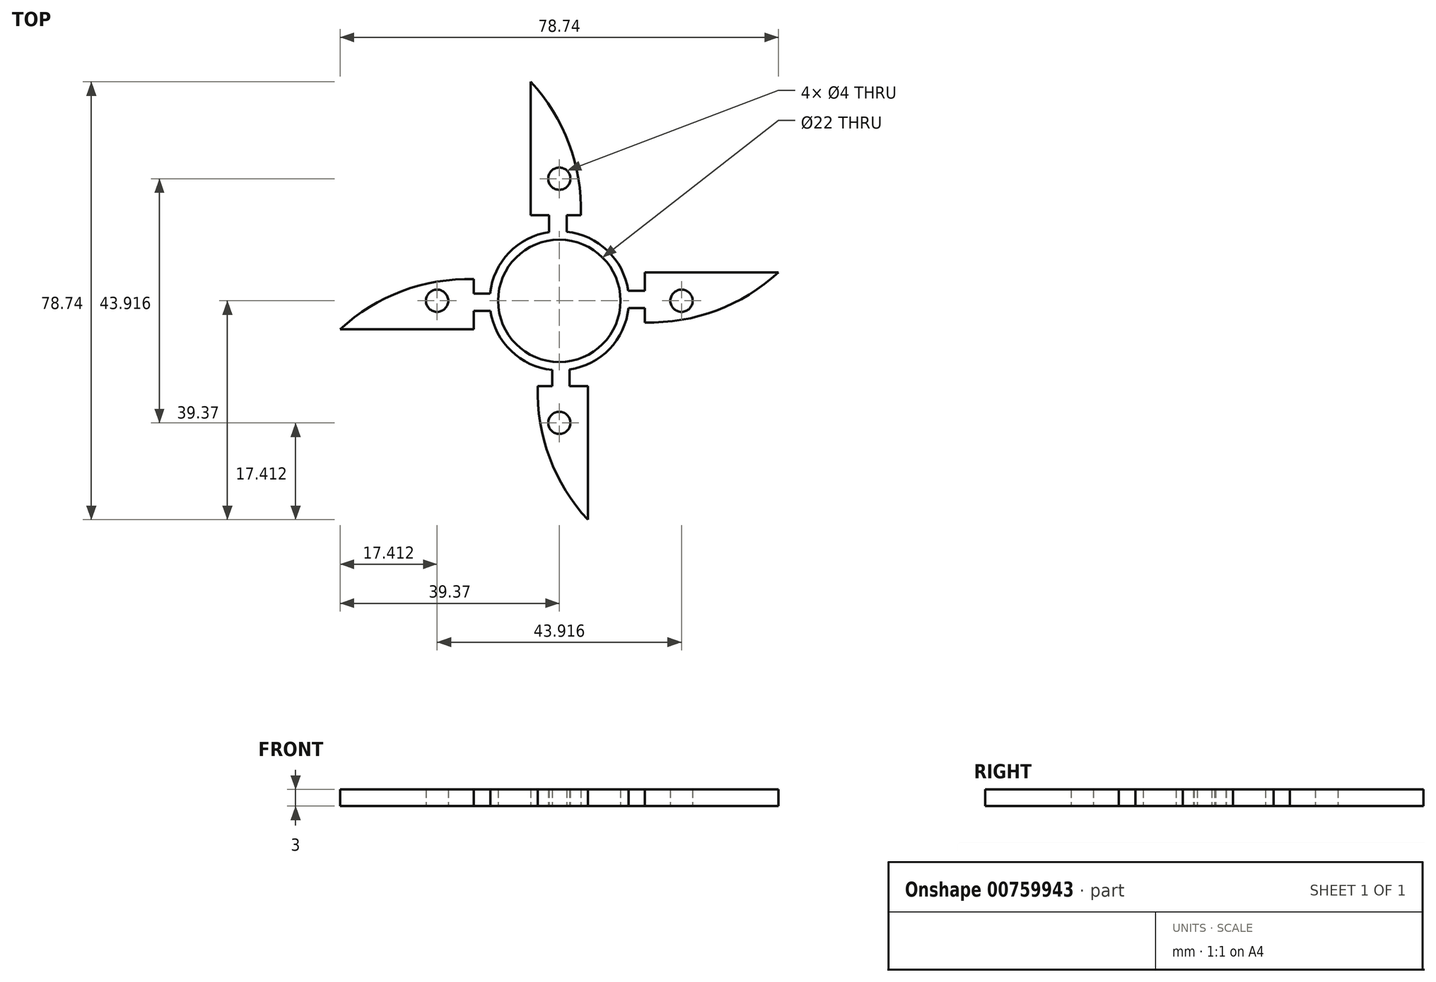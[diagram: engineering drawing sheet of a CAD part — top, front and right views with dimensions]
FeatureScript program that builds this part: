
annotation { "Feature Type Name" : "Feature", "Feature Type Description" : "" }
export const myFeature = defineFeature(function(context is Context, id is Id, definition is map)
    precondition{}
    {
        {
            var Q0;
            Q0=qCreatedBy(makeId("Top.planeOp"),FACE);
            var sketch = newSketch(context, id + "F0", { "sketchPlane" : qUnion([Q0])});
            skCircle(sketch, "E0", {"center": v(0, 0) * mm, "radius": 11 * mm});
            skCircle(sketch, "E1", {"center": v(0, 0) * mm, "radius": 12.5 * mm});
            skLineSegment(sketch, "E2", {"start": v(-1.82, 12.37) * mm, "end": v(-1.82, 15.37) * mm});
            skLineSegment(sketch, "E3", {"start": v(1.3, 12.43) * mm, "end": v(1.3, 15.43) * mm});
            skLineSegment(sketch, "E4", {"start": v(3.88, 15.37) * mm, "end": v(-5.12, 15.37) * mm});
            skLineSegment(sketch, "E5", {"start": v(-5.12, 15.37) * mm, "end": v(-5.12, 39.37) * mm});
            skArc(sketch, "E6", {"start": v(3.88, 15.37) * mm, "mid": v(1.74, 28.25) * mm, "end": v(-5.12, 39.37) * mm});
            skCircle(sketch, "E7", {"center": v(0, 21.96) * mm, "radius": 2 * mm});
            skArc(sketch, "E8.1.0", {"start": v(-15.37, 3.88) * mm, "mid": v(-28.25, 1.74) * mm, "end": v(-39.37, -5.12) * mm});
            skLineSegment(sketch, "E8.1.3", {"start": v(-15.37, -5.12) * mm, "end": v(-39.37, -5.12) * mm});
            skLineSegment(sketch, "E8.1.4", {"start": v(-12.37, -1.82) * mm, "end": v(-15.37, -1.82) * mm});
            skLineSegment(sketch, "E8.1.5", {"start": v(-12.43, 1.3) * mm, "end": v(-15.43, 1.3) * mm});
            skLineSegment(sketch, "E8.1.6", {"start": v(-15.37, 3.88) * mm, "end": v(-15.37, -5.12) * mm});
            skCircle(sketch, "E8.1.7", {"center": v(-21.96, 0) * mm, "radius": 2 * mm});
            skArc(sketch, "E8.2.0", {"start": v(-3.88, -15.37) * mm, "mid": v(-1.74, -28.25) * mm, "end": v(5.12, -39.37) * mm});
            skLineSegment(sketch, "E8.2.3", {"start": v(5.12, -15.37) * mm, "end": v(5.12, -39.37) * mm});
            skLineSegment(sketch, "E8.2.4", {"start": v(1.82, -12.37) * mm, "end": v(1.82, -15.37) * mm});
            skLineSegment(sketch, "E8.2.5", {"start": v(-1.3, -12.43) * mm, "end": v(-1.3, -15.43) * mm});
            skLineSegment(sketch, "E8.2.6", {"start": v(-3.88, -15.37) * mm, "end": v(5.12, -15.37) * mm});
            skCircle(sketch, "E8.2.7", {"center": v(0, -21.96) * mm, "radius": 2 * mm});
            skArc(sketch, "E8.3.0", {"start": v(15.37, -3.88) * mm, "mid": v(28.25, -1.74) * mm, "end": v(39.37, 5.12) * mm});
            skLineSegment(sketch, "E8.3.3", {"start": v(15.37, 5.12) * mm, "end": v(39.37, 5.12) * mm});
            skLineSegment(sketch, "E8.3.4", {"start": v(12.37, 1.82) * mm, "end": v(15.37, 1.82) * mm});
            skLineSegment(sketch, "E8.3.5", {"start": v(12.43, -1.3) * mm, "end": v(15.43, -1.3) * mm});
            skLineSegment(sketch, "E8.3.6", {"start": v(15.37, -3.88) * mm, "end": v(15.37, 5.12) * mm});
            skCircle(sketch, "E8.3.7", {"center": v(21.96, 0) * mm, "radius": 2 * mm});
            skSolve(sketch);
        }
        {
            var Q0;
            {var subQ0=sQuery(id+"F0.wireOp",EDGE,"E5");Q0=makeQuery(id+"F0.imprint","IMPRINT",FACE,{"disambiguationData":[TD([[makeQuery(id+"F0.imprint","IMPRINT",EDGE,{"derivedFrom":subQ0}),-1.0]])]});}
            var Q1;
            {var subQ0=sQuery(id+"F0.wireOp",EDGE,"E2");Q1=makeQuery(id+"F0.imprint","IMPRINT",FACE,{"disambiguationData":[TD([[makeQuery(id+"F0.imprint","IMPRINT",EDGE,{"derivedFrom":subQ0}),-1.0]])]});}
            var Q2;
            Q2=makeQuery(id+"F0.imprint","IMPRINT",FACE,{"disambiguationData":[TD([[makeQuery(id+"F0.imprint","IMPRINT",EDGE,{"derivedFrom":sQuery(id+"F0.wireOp",EDGE,"E0")}),-1.0]])]});
            var Q3;
            {var subQ3=sQuery(id+"F0.wireOp",EDGE,"E8.3.0");Q3=makeQuery(id+"F0.imprint","IMPRINT",FACE,{"disambiguationData":[TD([[makeQuery(id+"F0.imprint","IMPRINT",EDGE,{"derivedFrom":subQ3}),1.0]])]});}
            var Q4;
            {var subQ0=sQuery(id+"F0.wireOp",EDGE,"E8.2.4");Q4=makeQuery(id+"F0.imprint","IMPRINT",FACE,{"disambiguationData":[TD([[makeQuery(id+"F0.imprint","IMPRINT",EDGE,{"derivedFrom":subQ0}),-1.0]])]});}
            var Q5;
            {var subQ1=sQuery(id+"F0.wireOp",EDGE,"E8.2.0");Q5=makeQuery(id+"F0.imprint","IMPRINT",FACE,{"disambiguationData":[TD([[makeQuery(id+"F0.imprint","IMPRINT",EDGE,{"derivedFrom":subQ1}),1.0]])]});}
            var Q6;
            {var subQ1=sQuery(id+"F0.wireOp",EDGE,"E8.1.0");Q6=makeQuery(id+"F0.imprint","IMPRINT",FACE,{"disambiguationData":[TD([[makeQuery(id+"F0.imprint","IMPRINT",EDGE,{"derivedFrom":subQ1}),1.0]])]});}
            var Q7;
            {var subQ0=sQuery(id+"F0.wireOp",EDGE,"E8.1.4");Q7=makeQuery(id+"F0.imprint","IMPRINT",FACE,{"disambiguationData":[TD([[makeQuery(id+"F0.imprint","IMPRINT",EDGE,{"derivedFrom":subQ0}),-1.0]])]});}
            var Q8;
            {var subQ0=sQuery(id+"F0.wireOp",EDGE,"E8.3.4");Q8=makeQuery(id+"F0.imprint","IMPRINT",FACE,{"disambiguationData":[TD([[makeQuery(id+"F0.imprint","IMPRINT",EDGE,{"derivedFrom":subQ0}),-1.0]])]});}
            extrude(context, id + "F1", {"entities" : qUnion([Q0, Q1, Q2, Q3, Q4, Q5, Q6, Q7, Q8]), "depth" : 3 * mm, "offsetDistance" : 25 * mm});
        }
    });
